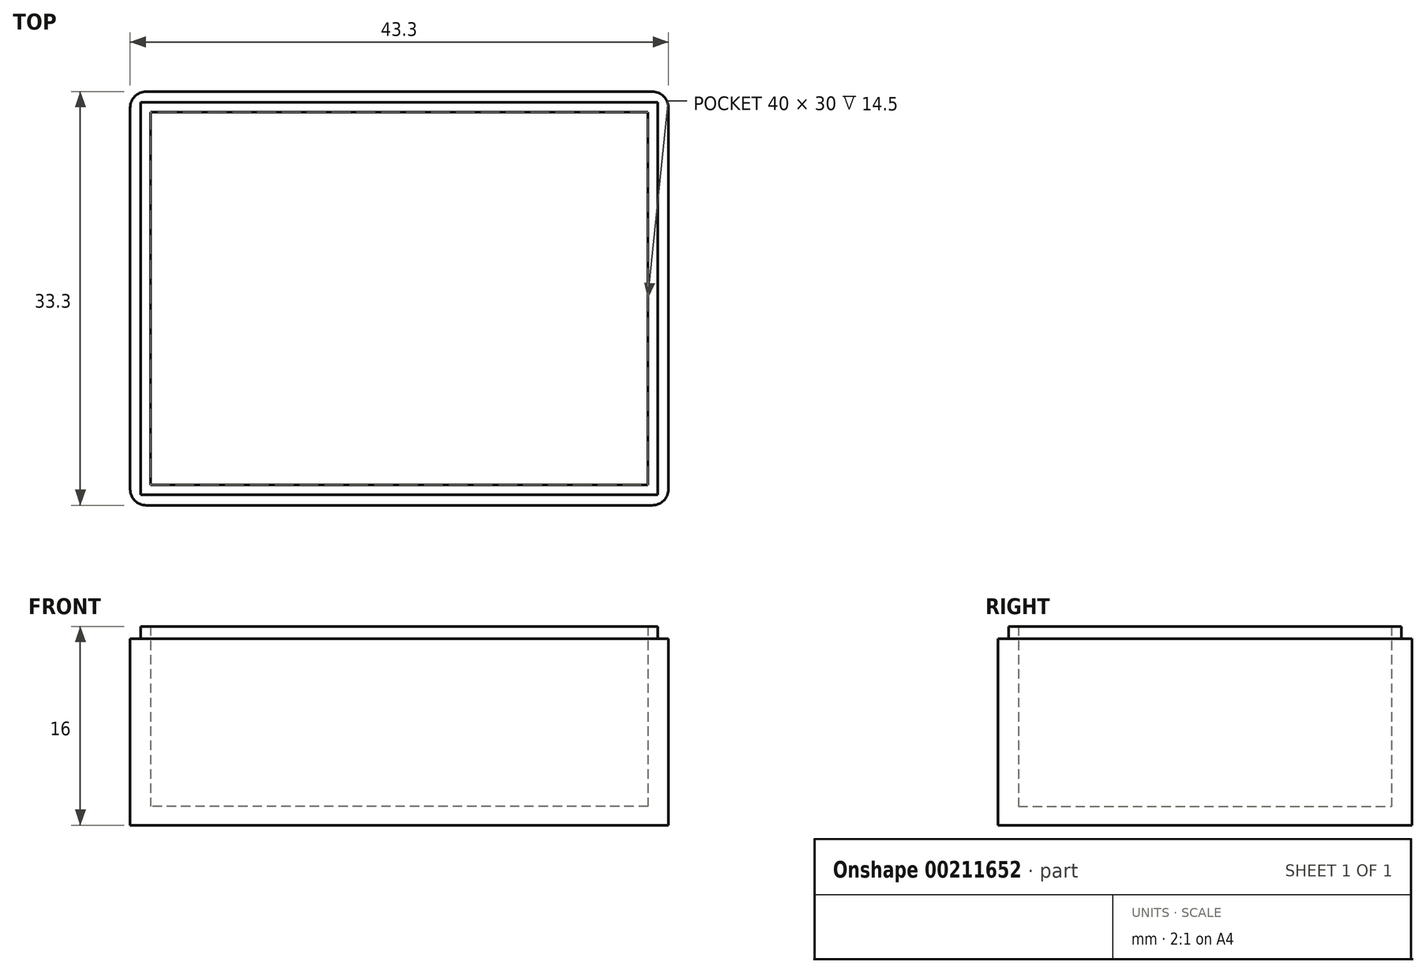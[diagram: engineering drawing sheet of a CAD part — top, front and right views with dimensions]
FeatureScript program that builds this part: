
annotation { "Feature Type Name" : "Feature", "Feature Type Description" : "" }
export const myFeature = defineFeature(function(context is Context, id is Id, definition is map)
    precondition{}
    {
        {
            var Q0;
            Q0=qCreatedBy(makeId("Top.planeOp"),FACE);
            var sketch = newSketch(context, id + "F0", { "sketchPlane" : qUnion([Q0])});
            skLineSegment(sketch, "E0.bottom", {"start": v(20, -15) * mm, "end": v(-20, -15) * mm});
            skLineSegment(sketch, "E0.top", {"start": v(20, 15) * mm, "end": v(-20, 15) * mm});
            skLineSegment(sketch, "E0.left", {"start": v(20, -15) * mm, "end": v(20, 15) * mm});
            skLineSegment(sketch, "E0.right", {"start": v(-20, -15) * mm, "end": v(-20, 15) * mm});
            skPoint(sketch, "E0.middle", {"position": v(0, 0) * mm});
            skLineSegment(sketch, "E1.0", {"start": v(21.65, -16.65) * mm, "end": v(-21.65, -16.65) * mm});
            skLineSegment(sketch, "E1.1", {"start": v(21.65, -16.65) * mm, "end": v(21.65, 16.65) * mm});
            skLineSegment(sketch, "E1.2", {"start": v(21.65, 16.65) * mm, "end": v(-21.65, 16.65) * mm});
            skLineSegment(sketch, "E1.3", {"start": v(-21.65, -16.65) * mm, "end": v(-21.65, 16.65) * mm});
            skSolve(sketch);
        }
        {
            var Q0;
            Q0=makeQuery(id+"F0.imprint","IMPRINT",FACE,{"disambiguationData":[TD([[makeQuery(id+"F0.imprint","IMPRINT",EDGE,{"derivedFrom":sQuery(id+"F0.wireOp",EDGE,"E0.bottom")}),1.0]])]});
            extrude(context, id + "F1", {"entities" : qUnion([Q0]), "depth" : 15 * mm});
        }
        {
            var Q0;
            Q0=makeQuery(id+"F0.imprint","IMPRINT",FACE,{"disambiguationData":[TD([[makeQuery(id+"F0.imprint","IMPRINT",EDGE,{"derivedFrom":sQuery(id+"F0.wireOp",EDGE,"E0.bottom")}),-1.0]])]});
            extrude(context, id + "F2", {"entities" : qUnion([Q0]), "operationType" : NewBodyOperationType.ADD, "depth" : 1.5 * mm});
        }
        {
            var Q0;
            Q0=makeQuery(id+"F1.opExtrude","CAP_FACE",FACE,{"disambiguationData":[OSD([sQuery(id+"F0.wireOp",EDGE,"E0.bottom"),sQuery(id+"F0.wireOp",EDGE,"E0.top"),sQuery(id+"F0.wireOp",EDGE,"E0.left"),sQuery(id+"F0.wireOp",EDGE,"E0.right"),sQuery(id+"F0.wireOp",EDGE,"E1.0"),sQuery(id+"F0.wireOp",EDGE,"E1.1"),sQuery(id+"F0.wireOp",EDGE,"E1.2"),sQuery(id+"F0.wireOp",EDGE,"E1.3")])],"isStart":false});
            var sketch = newSketch(context, id + "F3", { "sketchPlane" : qUnion([Q0])});
            skLineSegment(sketch, "E2.0", {"start": v(-20.8, -15.8) * mm, "end": v(-20.8, 15.8) * mm});
            skLineSegment(sketch, "E2.1", {"start": v(20.8, -15.8) * mm, "end": v(-20.8, -15.8) * mm});
            skLineSegment(sketch, "E2.2", {"start": v(20.8, -15.8) * mm, "end": v(20.8, 15.8) * mm});
            skLineSegment(sketch, "E2.3", {"start": v(20.8, 15.8) * mm, "end": v(-20.8, 15.8) * mm});
            skLineSegment(sketch, "E3", {"start": v(-20, -15) * mm, "end": v(-20, 15) * mm});
            skLineSegment(sketch, "E4", {"start": v(-20, 15) * mm, "end": v(20, 15) * mm});
            skLineSegment(sketch, "E5", {"start": v(20, 15) * mm, "end": v(20, -15) * mm});
            skLineSegment(sketch, "E6", {"start": v(20, -15) * mm, "end": v(-20, -15) * mm});
            skSolve(sketch);
        }
        {
            var Q0;
            Q0 = qSketchRegion(id + "F3", true);
            extrude(context, id + "F4", {"entities" : qUnion([Q0]), "operationType" : NewBodyOperationType.ADD, "depth" : 1 * mm});
        }
        {
            var Q0;
            Q0=makeQuery(id+"F1.opExtrude","SWEPT_EDGE",EDGE,{"disambiguationData":[OSD([sQuery(id+"F0.wireOp",EDGE,"E1.0"),sQuery(id+"F0.wireOp",EDGE,"E1.3")])]});
            var Q1;
            Q1=makeQuery(id+"F1.opExtrude","SWEPT_EDGE",EDGE,{"disambiguationData":[OSD([sQuery(id+"F0.wireOp",EDGE,"E1.0"),sQuery(id+"F0.wireOp",EDGE,"E1.1")])]});
            var Q2;
            Q2=makeQuery(id+"F1.opExtrude","SWEPT_EDGE",EDGE,{"disambiguationData":[OSD([sQuery(id+"F0.wireOp",EDGE,"E1.1"),sQuery(id+"F0.wireOp",EDGE,"E1.2")])]});
            var Q3;
            Q3=makeQuery(id+"F1.opExtrude","SWEPT_EDGE",EDGE,{"disambiguationData":[OSD([sQuery(id+"F0.wireOp",EDGE,"E1.2"),sQuery(id+"F0.wireOp",EDGE,"E1.3")])]});
            fillet(context, id + "F5", {"entities" : qUnion([Q0, Q1, Q2, Q3]), "radius" : 1.3 * mm, "tangentPropagation" : true, "allowEdgeOverflow" : false});
        }
    });
